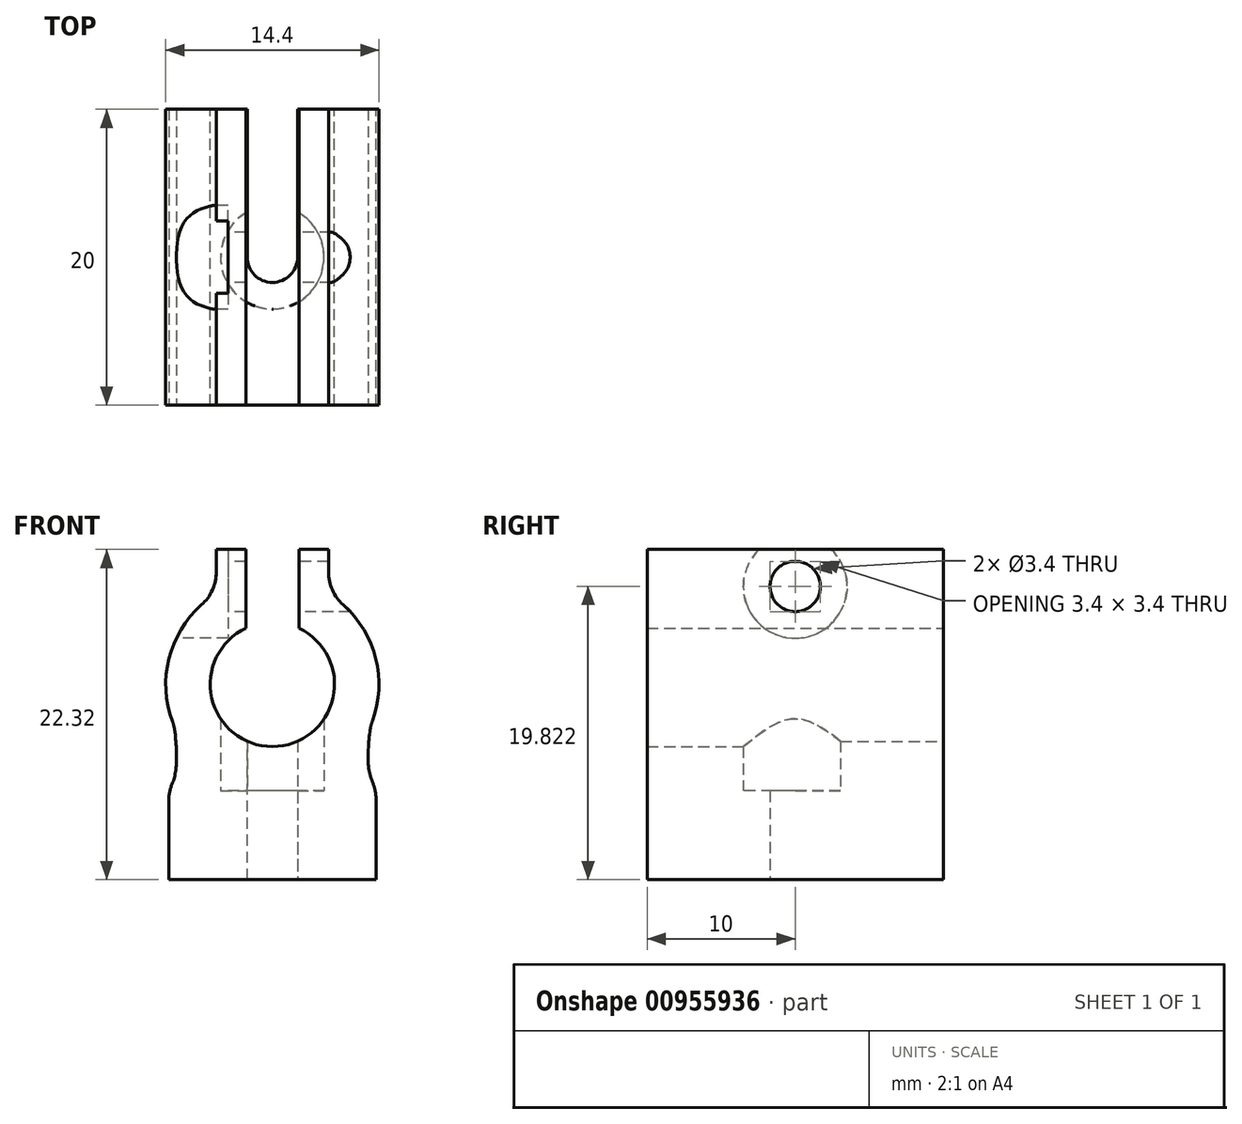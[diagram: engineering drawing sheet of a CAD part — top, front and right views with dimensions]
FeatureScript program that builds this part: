
annotation { "Feature Type Name" : "Feature", "Feature Type Description" : "" }
export const myFeature = defineFeature(function(context is Context, id is Id, definition is map)
    precondition{}
    {
        {
            var Q0;
            Q0=qCreatedBy(makeId("Front.planeOp"),FACE);
            var sketch = newSketch(context, id + "F0", { "sketchPlane" : qUnion([Q0])});
            skArc(sketch, "E0", {"start": v(-1.79, 3.8) * mm, "mid": v(0, -4.2) * mm, "end": v(1.79, 3.8) * mm});
            skArc(sketch, "E1", {"start": v(-3.79, 6.12) * mm, "mid": v(-6.86, 2.19) * mm, "end": v(-6.64, -2.8) * mm});
            skLineSegment(sketch, "E2", {"start": v(3.79, 9.12) * mm, "end": v(3.79, 6.12) * mm});
            skLineSegment(sketch, "E3", {"start": v(-1.79, 9.12) * mm, "end": v(-1.79, 3.8) * mm});
            skLineSegment(sketch, "E4", {"start": v(1.79, 9.12) * mm, "end": v(1.79, 3.8) * mm});
            skLineSegment(sketch, "E5", {"start": v(-1.79, 9.12) * mm, "end": v(-3.79, 9.12) * mm});
            skLineSegment(sketch, "E6", {"start": v(-3.79, 6.12) * mm, "end": v(-3.79, 9.12) * mm});
            skLineSegment(sketch, "E7", {"start": v(1.79, 9.12) * mm, "end": v(3.79, 9.12) * mm});
            skLineSegment(sketch, "E8", {"start": v(-7, -7.2) * mm, "end": v(-7, -13.2) * mm});
            skLineSegment(sketch, "E9", {"start": v(-7, -13.2) * mm, "end": v(7, -13.2) * mm});
            skLineSegment(sketch, "E10", {"start": v(7, -7.2) * mm, "end": v(7, -13.2) * mm});
            skPoint(sketch, "E11.orphan", {"position": v(9.08, -13.2) * mm});
            skFitSpline(sketch, "E12", {"points": [v(-7, -7.2) * mm, v(-6.5, -5.54) * mm, v(-6.64, -2.8) * mm, v(-6.64, -2.77) * mm], "startDerivative": vector(1.57, 3.06) * mm, "endDerivative": vector(-0.17, 0.18) * mm});
            skFitSpline(sketch, "E13", {"points": [v(7, -7.2) * mm, v(6.5, -5.54) * mm, v(6.64, -2.8) * mm], "startDerivative": vector(-1.44, 3.48) * mm, "endDerivative": vector(0.64, 5.26) * mm});
            skArc(sketch, "E14.trimOffspring", {"start": v(6.64, -2.8) * mm, "mid": v(6.86, 2.19) * mm, "end": v(3.79, 6.12) * mm});
            skLineSegment(sketch, "E15", {"start": v(-1.7, -4.2) * mm, "end": v(-1.7, -3.84) * mm});
            skLineSegment(sketch, "E16", {"start": v(-1.7, -4.2) * mm, "end": v(-1.7, -13.2) * mm});
            skLineSegment(sketch, "E17", {"start": v(1.7, -4.2) * mm, "end": v(1.7, -3.84) * mm});
            skLineSegment(sketch, "E18", {"start": v(1.7, -4.2) * mm, "end": v(1.7, -13.2) * mm});
            skPoint(sketch, "E19.start.orphan", {"position": v(0, -4.2) * mm});
            skLineSegment(sketch, "E20", {"start": v(0, -4.2) * mm, "end": v(1.7, -4.2) * mm, "construction": true});
            skLineSegment(sketch, "E21", {"start": v(0, -4.2) * mm, "end": v(-1.7, -4.2) * mm, "construction": true});
            skSolve(sketch);
        }
        {
            var Q0;
            Q0=qSketchRegion(id+"F0",true);
            extrude(context, id + "F1", {"entities" : qUnion([Q0]), "depth" : 20 * mm, "offsetDistance" : 25 * mm});
        }
        {
            var Q0;
            Q0=makeQuery(id+"F1.opExtrude","SWEPT_FACE",FACE,{"disambiguationData":[OSD([sQuery(id+"F0.wireOp",EDGE,"E8")])]});
            var sketch = newSketch(context, id + "F2", { "sketchPlane" : qUnion([Q0])});
            skLineSegment(sketch, "E22", {"start": v(10, -13.2) * mm, "end": v(10, 6.62) * mm, "construction": true});
            skCircle(sketch, "E23", {"center": v(10, 6.62) * mm, "radius": 1.7 * mm});
            skCircle(sketch, "E24", {"center": v(10, 6.62) * mm, "radius": 3.5 * mm});
            skSolve(sketch);
        }
        {
            var Q0;
            Q0=makeQuery(id+"F2.imprint","IMPRINT",FACE,{"disambiguationData":[TD([[makeQuery(id+"F2.imprint","IMPRINT",EDGE,{"derivedFrom":sQuery(id+"F2.wireOp",EDGE,"E23")}),-1.0]])]});
            extrude(context, id + "F3", {"entities" : qUnion([Q0]), "operationType" : NewBodyOperationType.REMOVE, "oppositeDirection" : true, "depth" : 4 * mm});
        }
        {
            var Q0;
            Q0=makeQuery(id+"F2.imprint","IMPRINT",FACE,{"disambiguationData":[TD([[makeQuery(id+"F2.imprint","IMPRINT",EDGE,{"derivedFrom":sQuery(id+"F2.wireOp",EDGE,"E23")}),1.0]])]});
            extrude(context, id + "F4", {"entities" : qUnion([Q0]), "operationType" : NewBodyOperationType.REMOVE, "oppositeDirection" : true, "depth" : 25 * mm});
        }
        {
            var Q0;
            Q0=makeQuery(id+"F1.opExtrude","SWEPT_EDGE",EDGE,{"disambiguationData":[OSD([sQuery(id+"F0.wireOp",EDGE,"E1"),sQuery(id+"F0.wireOp",EDGE,"E12")])]});
            var Q1;
            Q1=makeQuery(id+"F1.opExtrude","SWEPT_EDGE",EDGE,{"disambiguationData":[OSD([sQuery(id+"F0.wireOp",EDGE,"E13"),sQuery(id+"F0.wireOp",EDGE,"E14.trimOffspring")])]});
            var Q2;
            Q2=makeQuery(id+"F1.opExtrude","SWEPT_EDGE",EDGE,{"disambiguationData":[OSD([sQuery(id+"F0.wireOp",EDGE,"E8"),sQuery(id+"F0.wireOp",EDGE,"E12")])]});
            var Q3;
            Q3=makeQuery(id+"F1.opExtrude","SWEPT_EDGE",EDGE,{"disambiguationData":[OSD([sQuery(id+"F0.wireOp",EDGE,"E10"),sQuery(id+"F0.wireOp",EDGE,"E13")])]});
            var Q4;
            {var subQ0=sQuery(id+"F0.wireOp",EDGE,"E14.trimOffspring");var subQ1=sQuery(id+"F0.wireOp",EDGE,"E2");Q4=makeQuery(id+"F4.boolean.opBoolean","SPLIT",EDGE,{"disambiguationData":[TD([makeQuery(id+"F1.opExtrude","CAP_FACE",FACE,{"disambiguationData":[OSD([sQuery(id+"F0.wireOp",EDGE,"E0"),sQuery(id+"F0.wireOp",EDGE,"E1"),subQ1,sQuery(id+"F0.wireOp",EDGE,"E3"),sQuery(id+"F0.wireOp",EDGE,"E4"),sQuery(id+"F0.wireOp",EDGE,"E5"),sQuery(id+"F0.wireOp",EDGE,"E6"),sQuery(id+"F0.wireOp",EDGE,"E7"),sQuery(id+"F0.wireOp",EDGE,"E8"),sQuery(id+"F0.wireOp",EDGE,"E9"),sQuery(id+"F0.wireOp",EDGE,"E10"),sQuery(id+"F0.wireOp",EDGE,"E12"),sQuery(id+"F0.wireOp",EDGE,"E13"),subQ0])],"isStart":false})])],"derivedFrom":makeQuery(id+"F1.opExtrude","SWEPT_EDGE",EDGE,{"disambiguationData":[OSD([subQ1,subQ0])]})});}
            var Q5;
            {var subQ0=sQuery(id+"F0.wireOp",EDGE,"E14.trimOffspring");var subQ1=sQuery(id+"F0.wireOp",EDGE,"E2");Q5=makeQuery(id+"F4.boolean.opBoolean","SPLIT",EDGE,{"disambiguationData":[TD([makeQuery(id+"F1.opExtrude","CAP_FACE",FACE,{"disambiguationData":[OSD([sQuery(id+"F0.wireOp",EDGE,"E0"),sQuery(id+"F0.wireOp",EDGE,"E1"),subQ1,sQuery(id+"F0.wireOp",EDGE,"E3"),sQuery(id+"F0.wireOp",EDGE,"E4"),sQuery(id+"F0.wireOp",EDGE,"E5"),sQuery(id+"F0.wireOp",EDGE,"E6"),sQuery(id+"F0.wireOp",EDGE,"E7"),sQuery(id+"F0.wireOp",EDGE,"E8"),sQuery(id+"F0.wireOp",EDGE,"E9"),sQuery(id+"F0.wireOp",EDGE,"E10"),sQuery(id+"F0.wireOp",EDGE,"E12"),sQuery(id+"F0.wireOp",EDGE,"E13"),subQ0])],"isStart":true})])],"derivedFrom":makeQuery(id+"F1.opExtrude","SWEPT_EDGE",EDGE,{"disambiguationData":[OSD([subQ1,subQ0])]})});}
            var Q6;
            {var subQ0=sQuery(id+"F0.wireOp",EDGE,"E6");var subQ1=sQuery(id+"F0.wireOp",EDGE,"E1");Q6=makeQuery(id+"F3.boolean.opBoolean","SPLIT",EDGE,{"disambiguationData":[TD([makeQuery(id+"F1.opExtrude","CAP_FACE",FACE,{"disambiguationData":[OSD([sQuery(id+"F0.wireOp",EDGE,"E0"),subQ1,sQuery(id+"F0.wireOp",EDGE,"E2"),sQuery(id+"F0.wireOp",EDGE,"E3"),sQuery(id+"F0.wireOp",EDGE,"E4"),sQuery(id+"F0.wireOp",EDGE,"E5"),subQ0,sQuery(id+"F0.wireOp",EDGE,"E7"),sQuery(id+"F0.wireOp",EDGE,"E8"),sQuery(id+"F0.wireOp",EDGE,"E9"),sQuery(id+"F0.wireOp",EDGE,"E10"),sQuery(id+"F0.wireOp",EDGE,"E12"),sQuery(id+"F0.wireOp",EDGE,"E13"),sQuery(id+"F0.wireOp",EDGE,"E14.trimOffspring")])],"isStart":true})])],"derivedFrom":makeQuery(id+"F1.opExtrude","SWEPT_EDGE",EDGE,{"disambiguationData":[OSD([subQ1,subQ0])]})});}
            var Q7;
            {var subQ0=sQuery(id+"F0.wireOp",EDGE,"E6");var subQ1=sQuery(id+"F0.wireOp",EDGE,"E1");Q7=makeQuery(id+"F3.boolean.opBoolean","SPLIT",EDGE,{"disambiguationData":[TD([makeQuery(id+"F1.opExtrude","CAP_FACE",FACE,{"disambiguationData":[OSD([sQuery(id+"F0.wireOp",EDGE,"E0"),subQ1,sQuery(id+"F0.wireOp",EDGE,"E2"),sQuery(id+"F0.wireOp",EDGE,"E3"),sQuery(id+"F0.wireOp",EDGE,"E4"),sQuery(id+"F0.wireOp",EDGE,"E5"),subQ0,sQuery(id+"F0.wireOp",EDGE,"E7"),sQuery(id+"F0.wireOp",EDGE,"E8"),sQuery(id+"F0.wireOp",EDGE,"E9"),sQuery(id+"F0.wireOp",EDGE,"E10"),sQuery(id+"F0.wireOp",EDGE,"E12"),sQuery(id+"F0.wireOp",EDGE,"E13"),sQuery(id+"F0.wireOp",EDGE,"E14.trimOffspring")])],"isStart":false})])],"derivedFrom":makeQuery(id+"F1.opExtrude","SWEPT_EDGE",EDGE,{"disambiguationData":[OSD([subQ1,subQ0])]})});}
            fillet(context, id + "F5", {"entities" : qUnion([Q0, Q1, Q2, Q3, Q4, Q5, Q6, Q7]), "radius" : 3 * mm, "tangentPropagation" : true, "allowEdgeOverflow" : false});
        }
        {
            var Q0;
            Q0=makeQuery(id+"F1.opExtrude","SWEPT_FACE",FACE,{"disambiguationData":[OSD([sQuery(id+"F0.wireOp",EDGE,"E9")])]});
            var sketch = newSketch(context, id + "F6", { "sketchPlane" : qUnion([Q0])});
            skLineSegment(sketch, "E25", {"start": v(-7, 10) * mm, "end": v(0, 10) * mm, "construction": true});
            skCircle(sketch, "E26", {"center": v(0, 10) * mm, "radius": 1.7 * mm});
            skCircle(sketch, "E27", {"center": v(0, 10) * mm, "radius": 3.5 * mm});
            skSolve(sketch);
        }
        {
            var Q0;
            Q0=makeQuery(id+"F6.imprint","IMPRINT",FACE,{"disambiguationData":[TD([[makeQuery(id+"F6.imprint","IMPRINT",EDGE,{"derivedFrom":sQuery(id+"F6.wireOp",EDGE,"E26")}),-1.0]])]});
            extrude(context, id + "F7", {"entities" : qUnion([Q0]), "operationType" : NewBodyOperationType.REMOVE, "oppositeDirection" : true, "depth" : 12 * mm});
        }
        {
            var Q0;
            Q0=makeQuery(id+"F7.boolean.opBoolean","SPLIT",FACE,{"disambiguationData":[TD([makeQuery(id+"F7.opExtrude","SWEPT_FACE",FACE,{"disambiguationData":[OSD([sQuery(id+"F6.wireOp",EDGE,"E26")])]})])],"derivedFrom":makeQuery(id+"F1.opExtrude","SWEPT_FACE",FACE,{"disambiguationData":[OSD([sQuery(id+"F0.wireOp",EDGE,"E9")])]})});
            extrude(context, id + "F8", {"entities" : qUnion([Q0]), "operationType" : NewBodyOperationType.REMOVE, "oppositeDirection" : true, "depth" : 12 * mm});
        }
        {
            var Q0;
            Q0=makeQuery(id+"F6.imprint","IMPRINT",FACE,{"disambiguationData":[TD([[makeQuery(id+"F6.imprint","IMPRINT",EDGE,{"derivedFrom":sQuery(id+"F6.wireOp",EDGE,"E26")}),-1.0]])]});
            extrude(context, id + "F9", {"entities" : qUnion([Q0]), "operationType" : NewBodyOperationType.ADD, "oppositeDirection" : true, "depth" : 6 * mm});
        }
        {
            var Q0;
            {var subQ0=sQuery(id+"F0.wireOp",EDGE,"E15");Q0=makeQuery(id+"F0.imprint","IMPRINT",FACE,{"disambiguationData":[TD([[makeQuery(id+"F0.imprint","IMPRINT",EDGE,{"derivedFrom":subQ0}),-1.0]])]});}
            extrude(context, id + "F10", {"entities" : qUnion([Q0]), "operationType" : NewBodyOperationType.REMOVE, "depth" : 10 * mm});
        }
    });
